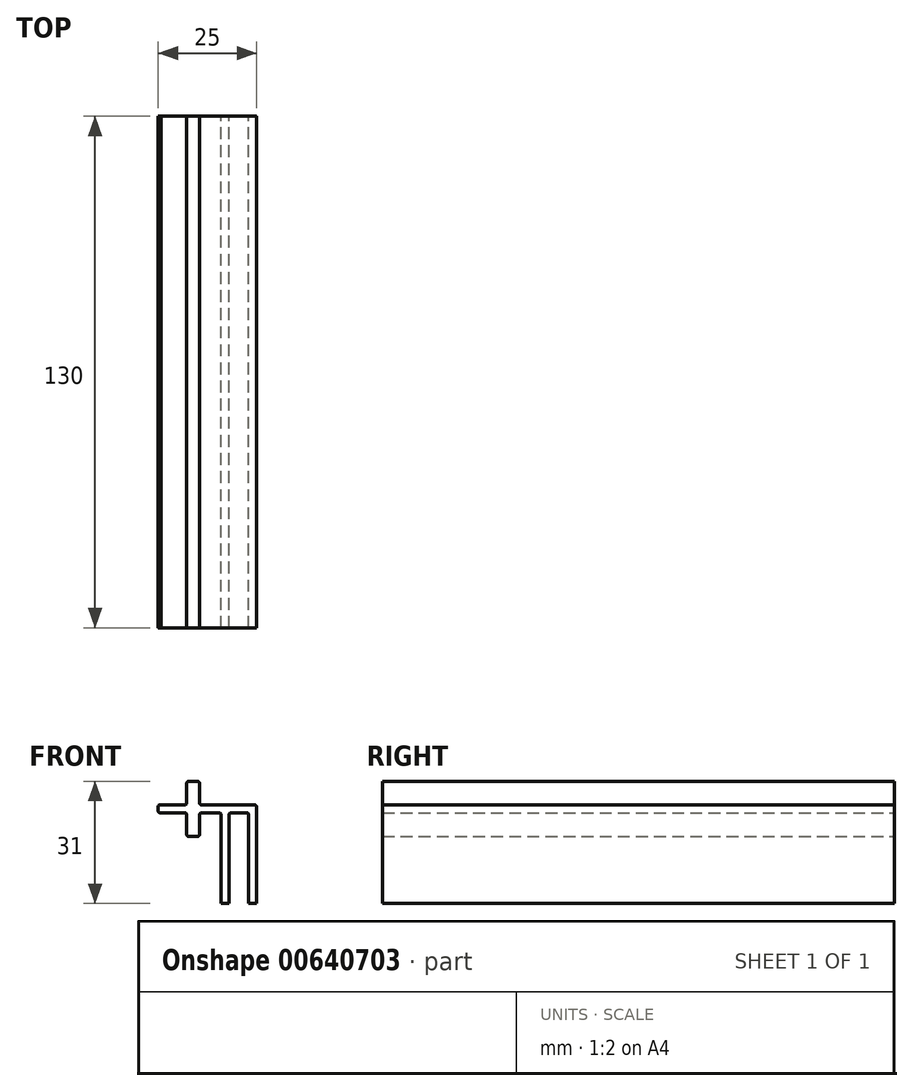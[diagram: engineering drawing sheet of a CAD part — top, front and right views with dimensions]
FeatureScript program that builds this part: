
annotation { "Feature Type Name" : "Feature", "Feature Type Description" : "" }
export const myFeature = defineFeature(function(context is Context, id is Id, definition is map)
    precondition{}
    {
        {
            var Q0;
            Q0=qCreatedBy(makeId("Front.planeOp"),FACE);
            var sketch = newSketch(context, id + "F0", { "sketchPlane" : qUnion([Q0])});
            skLineSegment(sketch, "E0", {"start": v(0, 0) * mm, "end": v(0, 24.5) * mm});
            skArc(sketch, "E1", {"start": v(0, 24.5) * mm, "mid": v(-0.15, 24.85) * mm, "end": v(-0.5, 25) * mm});
            skLineSegment(sketch, "E2", {"start": v(-2, 0) * mm, "end": v(-2, 22.5) * mm});
            skArc(sketch, "E3", {"start": v(-2, 22.5) * mm, "mid": v(-2.15, 22.85) * mm, "end": v(-2.5, 23) * mm});
            skLineSegment(sketch, "E4", {"start": v(-2.5, 23) * mm, "end": v(-6.5, 23) * mm});
            skArc(sketch, "E5", {"start": v(-6.5, 23) * mm, "mid": v(-6.85, 22.85) * mm, "end": v(-7, 22.5) * mm});
            skLineSegment(sketch, "E6", {"start": v(-7, 22.5) * mm, "end": v(-7, 0) * mm});
            skLineSegment(sketch, "E7", {"start": v(-9, 0) * mm, "end": v(-9, 22.5) * mm});
            skArc(sketch, "E8", {"start": v(-9, 22.5) * mm, "mid": v(-9.14, 22.85) * mm, "end": v(-9.5, 23) * mm});
            skLineSegment(sketch, "E9", {"start": v(-9.5, 23) * mm, "end": v(-14, 23) * mm});
            skArc(sketch, "E10", {"start": v(-14, 23) * mm, "mid": v(-14.35, 22.85) * mm, "end": v(-14.5, 22.5) * mm});
            skLineSegment(sketch, "E11", {"start": v(-14.5, 22.5) * mm, "end": v(-14.5, 17.5) * mm});
            skLineSegment(sketch, "E12", {"start": v(-0.5, 25) * mm, "end": v(-14, 25) * mm});
            skLineSegment(sketch, "E13", {"start": v(-17.75, 22.5) * mm, "end": v(-17.75, 17.5) * mm});
            skArc(sketch, "E14", {"start": v(-17.74, 17.5) * mm, "mid": v(-17.6, 17.15) * mm, "end": v(-17.24, 17) * mm});
            skArc(sketch, "E15", {"start": v(-15, 17) * mm, "mid": v(-14.64, 17.15) * mm, "end": v(-14.5, 17.5) * mm});
            skLineSegment(sketch, "E16", {"start": v(-15, 17) * mm, "end": v(-17.24, 17) * mm});
            skArc(sketch, "E17", {"start": v(-17.75, 22.5) * mm, "mid": v(-17.9, 22.85) * mm, "end": v(-18.25, 23) * mm});
            skLineSegment(sketch, "E18", {"start": v(-18.25, 23) * mm, "end": v(-24.5, 23) * mm});
            skArc(sketch, "E19", {"start": v(-25, 23.5) * mm, "mid": v(-24.85, 23.15) * mm, "end": v(-24.5, 23) * mm});
            skLineSegment(sketch, "E20", {"start": v(-25, 23.5) * mm, "end": v(-25, 24.56) * mm});
            skArc(sketch, "E21", {"start": v(-24.26, 25) * mm, "mid": v(-24.75, 25) * mm, "end": v(-25, 24.56) * mm});
            skLineSegment(sketch, "E22", {"start": v(-9, 0) * mm, "end": v(-7, 0) * mm});
            skLineSegment(sketch, "E23", {"start": v(-2, 0) * mm, "end": v(0, 0) * mm});
            skLineSegment(sketch, "E24", {"start": v(-16.12, 17) * mm, "end": v(-16.12, 31) * mm, "construction": true});
            skLineSegment(sketch, "E25", {"start": v(-14, 23) * mm, "end": v(-14, 25) * mm, "construction": true});
            skLineSegment(sketch, "E26", {"start": v(-9.5, 23) * mm, "end": v(-6.5, 23) * mm, "construction": true});
            skLineSegment(sketch, "E27", {"start": v(-18.25, 23) * mm, "end": v(-14, 23) * mm, "construction": true});
            skLineSegment(sketch, "E28", {"start": v(-24.26, 25) * mm, "end": v(-18.25, 25) * mm});
            skLineSegment(sketch, "E29", {"start": v(-18.25, 25) * mm, "end": v(-18.25, 23) * mm, "construction": true});
            skArc(sketch, "E30", {"start": v(-18.25, 25) * mm, "mid": v(-17.9, 25.15) * mm, "end": v(-17.75, 25.5) * mm});
            skArc(sketch, "E31", {"start": v(-14.5, 25.5) * mm, "mid": v(-14.35, 25.15) * mm, "end": v(-14, 25) * mm});
            skArc(sketch, "E32", {"start": v(-14.5, 30.5) * mm, "mid": v(-14.64, 30.85) * mm, "end": v(-15, 31) * mm});
            skArc(sketch, "E33", {"start": v(-17.25, 31) * mm, "mid": v(-17.6, 30.85) * mm, "end": v(-17.75, 30.5) * mm});
            skLineSegment(sketch, "E34", {"start": v(-17.74, 30.5) * mm, "end": v(-17.74, 25.5) * mm});
            skLineSegment(sketch, "E35", {"start": v(-17.25, 31) * mm, "end": v(-15, 31) * mm});
            skLineSegment(sketch, "E36", {"start": v(-14.5, 30.5) * mm, "end": v(-14.5, 25.5) * mm});
            skLineSegment(sketch, "E37", {"start": v(-18.25, 25) * mm, "end": v(-14, 25) * mm, "construction": true});
            skSolve(sketch);
        }
        {
            var Q0;
            Q0 = qSketchRegion(id + "F0", true);
            extrude(context, id + "F1", {"entities" : qUnion([Q0]), "depth" : 130 * mm, "offsetDistance" : 25 * mm});
        }
    });
